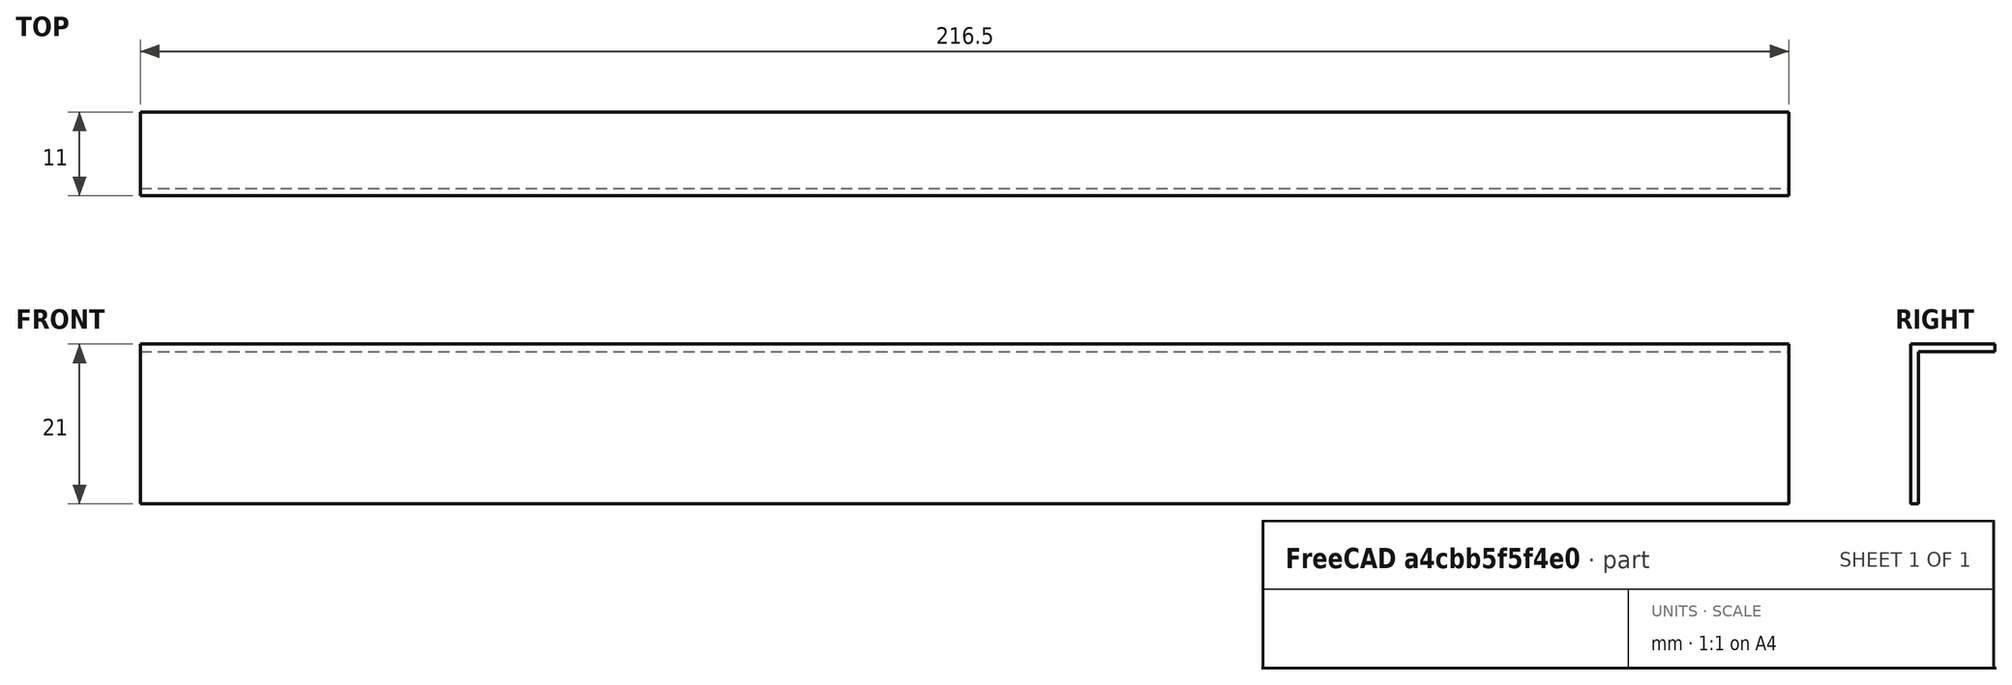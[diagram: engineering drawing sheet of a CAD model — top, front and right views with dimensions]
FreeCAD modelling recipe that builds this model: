
FCSTD DOCUMENT  (FreeCAD 0.21R33694 (Git))
Label: baguette-enjoliveur-raidisseur-banc
License: Creative Commons Attribution 3.0
LicenseURL: http://en.wikipedia.org/wiki/Public_domain
objects: Sketcher::SketchObject×1, PartDesign::Pad×1, PartDesign::Body×1
note: 4 computed .brp shape members not serialized (recipe doc carries the construction recipe); baked Part::Feature solids carry a one-line shape summary decoded from their .brp

FEATURE [Sketcher::SketchObject] Sketch
  FullyConstrained = true
  MapMode = 5
  Placement = pos=(0,0,0) rot=(0.57735,0.57735,0.57735;2.0944rad)
  Support = -> [YZ_Plane]
  sketch-geometry (6):
    g0: LineSegment StartX=1 StartY=20 StartZ=0 EndX=11 EndY=20 EndZ=0
    g1: LineSegment StartX=1 StartY=20 StartZ=0 EndX=1 EndY=0 EndZ=0
    g2: LineSegment StartX=11 StartY=20 StartZ=0 EndX=11 EndY=21 EndZ=0
    g3: LineSegment StartX=11 StartY=21 StartZ=0 EndX=0 EndY=21 EndZ=0
    g4: LineSegment StartX=0 StartY=21 StartZ=0 EndX=0 EndY=0 EndZ=0
    g5: LineSegment StartX=0 StartY=0 StartZ=0 EndX=1 EndY=0 EndZ=0
  constraints (17):
    c: Horizontal(g0)
    c: Coincident(g0,g1)
    c: Vertical(g1)
    c: Coincident(g0,g2)
    c: Coincident(g2,g3)
    c: Horizontal(g3)
    c: Coincident(g3,g4)
    c: Vertical(g4)
    c: Coincident(g4,g5)
    c: Coincident(g5,g1)
    c: DistanceY(g1,g1) = 20
    c: DistanceX(g0,g0) = 10
    c: Horizontal(g5)
    c: DistanceX(g5,g5) = 1
    c: Vertical(g2)
    c: DistanceY(g2,g2) = 1
    c: Coincident(g4,g-1)
FEATURE [PartDesign::Pad] Pad
  Direction = (1,-2e-16,3e-16)
  Length = 216.5
  Length2 = 10
  Placement = pos=(0,0,0) rot=(0.57735,0.57735,0.57735;2.0944rad)
  Profile = -> Sketch
  ReferenceAxis = -> Sketch [N_Axis]
  Type = 0
FEATURE [PartDesign::Body] Body
  Group = -> [Sketch,Pad]
  Origin = -> Origin
  Tip = -> Pad
